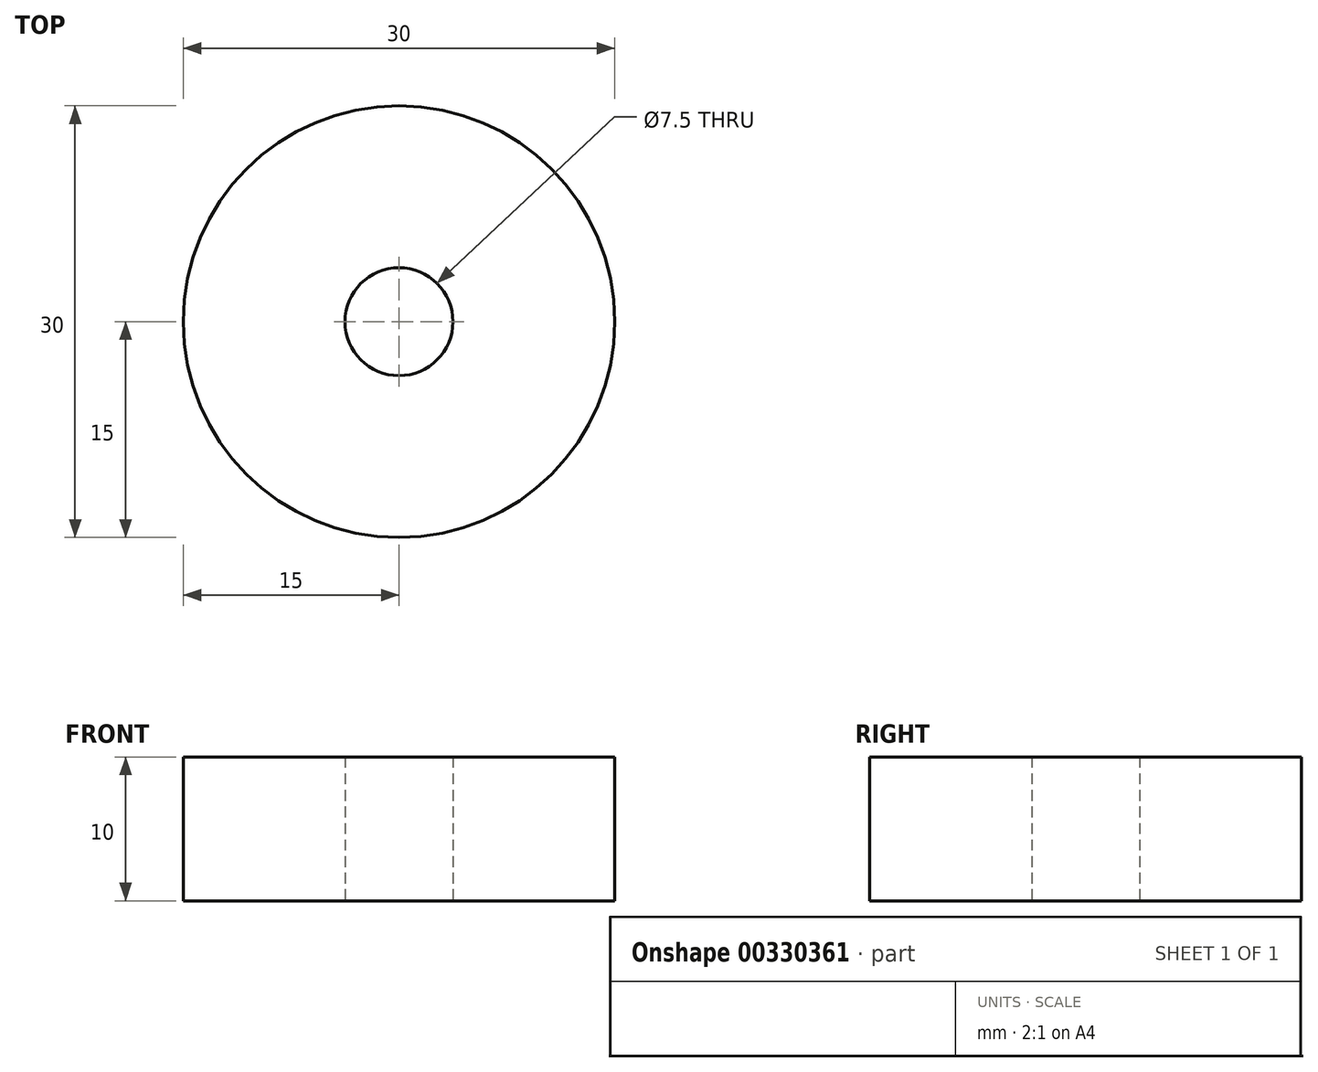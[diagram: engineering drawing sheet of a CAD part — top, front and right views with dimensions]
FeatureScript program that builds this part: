
annotation { "Feature Type Name" : "Feature", "Feature Type Description" : "" }
export const myFeature = defineFeature(function(context is Context, id is Id, definition is map)
    precondition{}
    {
        {
            var Q0;
            Q0=qCreatedBy(makeId("Top.planeOp"),FACE);
            var sketch = newSketch(context, id + "F0", { "sketchPlane" : qUnion([Q0])});
            skCircle(sketch, "E0", {"center": v(0, 0) * mm, "radius": 3.75 * mm});
            skCircle(sketch, "E1", {"center": v(0, 0) * mm, "radius": 15 * mm});
            skSolve(sketch);
        }
        {
            var Q0;
            Q0=makeQuery(id+"F0.imprint","IMPRINT",FACE,{"disambiguationData":[TD([[makeQuery(id+"F0.imprint","IMPRINT",EDGE,{"derivedFrom":sQuery(id+"F0.wireOp",EDGE,"E0")}),-1.0]])]});
            extrude(context, id + "F1", {"entities" : qUnion([Q0]), "depth" : 10 * mm});
        }
    });
